# Revit family: r2018_videomax_urm_stoechnogo_ispolneniya
name_source: partatom
category: Устройства связи
revit_build: Autodesk Revit 2018 (Build: 20181011_1500(x64)
units: mm (PartAtom-declared; Revit-internal decimal feet)

## family parameters
Общий = Нет
Основа = Грань
При загрузке вырезать с полостями = Нет
Размер круглого соединителя = Использовать диаметр
Сохранять ориентацию аннотаций = Да
Тип детали = Нормальный
Точка расчета площади = Нет

## types (3) — shared parameters
ADSK_Версия Revit = 2018
ADSK_Версия семейства = v2
ADSK_Единица измерения = шт.
ADSK_Завод-изготовитель = ООО «Видеомакс»
ADSK_Код изделия = ТУ 26.20.15-003-37165186-2020
ADSK_Количество = 1
ADSK_Коэффициент мощности = 0.96
ADSK_Марка = VIDEOMAX-URM
ADSK_Напряжение = 230 В
ADSK_Номинальная мощность = 0 В·А
ADSK_Ток = 0 А
Material = Черный
URL = https://www.videomax-server.ru
Изготовитель = ООО «Видеомакс»
Количество входов 230V, шт = 1
Количество интерфейсов Gigabit LAN, шт = 1
Максимальное количество подключаемых мониторов, шт = 1
Отметка по умолчанию = 2600 мм
zero-valued in all types: ADSK_Масса, Количество интерфейсов 10 Gigabit LAN, шт, Максимальная мощность БП, Вт, Максимальная потребляемая мощность Вт, Максимальное тепловыделение, BTU/h, Стоимость

## per-type parameters (varying)
| type | 19” 2U (2S) | 19” 3U (3S) | 19” 4U (4A) | ADSK_Наименование | Back | Front | Высота | Глубина | Изображение типоразмера | Минимальная глубина шкафа, мм | Указания по монтажу | Ширина |
| 19” 2U (2S) | Да | Нет | Нет | УРМ стоечного исполнения 19” 2U (2S) | videomax_OPS-SKUD_stoechnogo : Back | videomax_OPS-SKUD_stoechnogo : Front | 88 мм | 430 мм | 19 (2U.2S).png | 600 | Для монтажа использовать 19” салазки. Изделие комплектуется салазками SR20 либо SR26. Параметры SR20: расстояние между профилями 488 - 546 мм, габариты в сложенном состоянии 500 мм, параметры SR26: расстояние между профилями 572 - 672 мм, габариты в сложенном состоянии 650 мм. | 427 мм |
| 19” 4U (4A) | Нет | Нет | Да | УРМ стоечного исполнения 19” 4U (4A) | videomax_19 4U (4A) : Back | videomax_19 4U (4A) : Front | 176 мм | 450 мм | 19 4U (4A).jpg | 600 | Для монтажа использовать комплектные 19” салазки с параметрами: расстояние между профилями 488 - 546 мм, габариты в сложенном состоянии 500 мм | 430 мм |
| 19” 3U (3S) | Нет | Да | Нет | УРМ стоечного исполнения 19” 3U (3S) | videomax_19 3U (3S, 3N) : Back | videomax_19 3U (3S, 3N) : Front | 133 мм | 530 мм | 19 (3U.3S).png | 800 | Для монтажа использовать комплектные 19” салазки SR26 с параметрами: расстояние между профилями 572 - 672 мм, габариты в сложенном состоянии 650 мм. | 430 мм |

note: column(s) folded — value = type name in every type: ADSK_Обозначение
